# Revit family: IRB 250  E1 EC_7880013
name_source: partatom
category: Mechanical Equipment
revit_build: Autodesk Revit MEP 2014 (Build: 20130308_1515(x64)
units: mm (PartAtom-declared; Revit-internal decimal feet)

## types (1)
- IRB 250 E1 EC
    Capacitor = - µF
    Current = 1 A
    Depth = 410 mm  [stored 1.34514 ft]
    Description = Insulated duct fans with circular connections
    Diameter = 250 mm  [stored 0.82021 ft]
    Frequency = 50 Hz
    Height = 608 mm  [stored 1.99475 ft]
    Main Material = Steel, Galvanized
    Max. temperature of transported air = 60 °C
    Max. temperature of transported air when speed controlled = 60 °C
    Phase = 1
    Power = 311 W
    Sound pressure level at 3 m = 59 dB(A)
    Speed = 2020 rpm
    Voltage = 230 V
    Voltage range = 200-240 V
    Weight = 34.00 kg
    Width = 744 mm  [stored 2.44094 ft]
    Wiring diagram = 4040135

note: [stored X ft] marks values corroborated as IEEE doubles in the binary element streams (Revit-internal decimal feet)

## geometry (parser evidence)
native form markers: Sweep x2
no freeform markers — native parametric forms only
